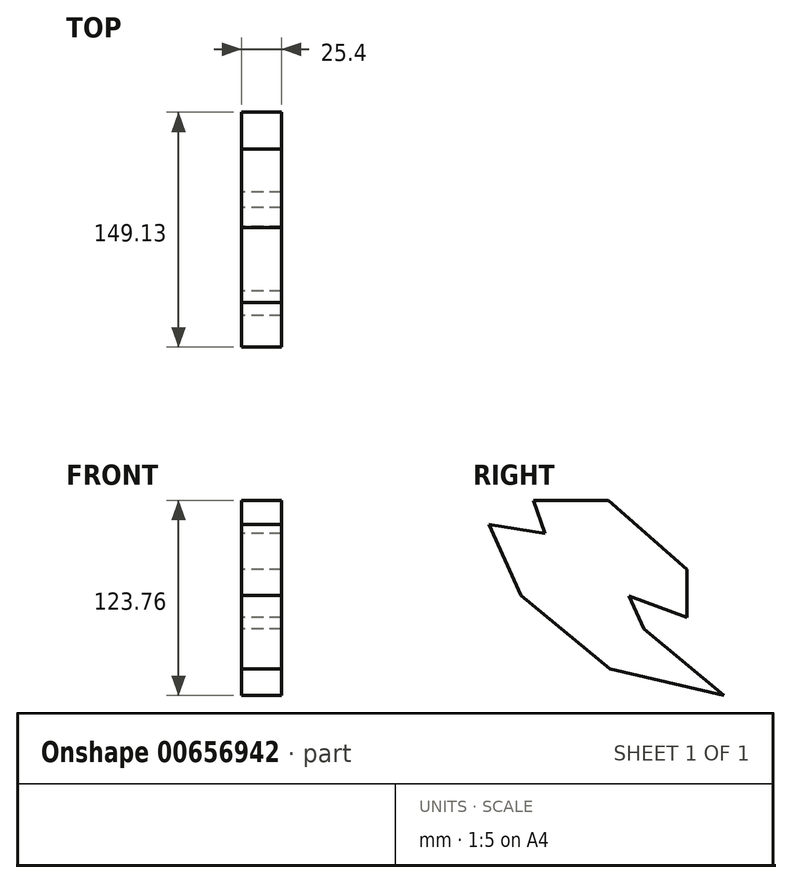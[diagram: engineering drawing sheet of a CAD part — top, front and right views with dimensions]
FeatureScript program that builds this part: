
annotation { "Feature Type Name" : "Feature", "Feature Type Description" : "" }
export const myFeature = defineFeature(function(context is Context, id is Id, definition is map)
    precondition{}
    {
        {
            var Q0;
            Q0=qCreatedBy(makeId("Right.planeOp"),FACE);
            var sketch = newSketch(context, id + "F0", { "sketchPlane" : qUnion([Q0])});
            skLineSegment(sketch, "E0", {"start": v(-23.38, 27.05) * mm, "end": v(24.18, 27.05) * mm});
            skLineSegment(sketch, "E1", {"start": v(24.18, 27.05) * mm, "end": v(74.16, -16.6) * mm});
            skLineSegment(sketch, "E2", {"start": v(74.16, -16.6) * mm, "end": v(74.16, -47.35) * mm});
            skLineSegment(sketch, "E3", {"start": v(74.16, -47.35) * mm, "end": v(37.08, -33.43) * mm});
            skLineSegment(sketch, "E4", {"start": v(37.08, -33.43) * mm, "end": v(46.75, -54.56) * mm});
            skLineSegment(sketch, "E5", {"start": v(46.75, -54.56) * mm, "end": v(97.54, -96.7) * mm});
            skLineSegment(sketch, "E6", {"start": v(97.54, -96.7) * mm, "end": v(24.99, -79.98) * mm});
            skLineSegment(sketch, "E7", {"start": v(24.99, -79.98) * mm, "end": v(-31.44, -33.15) * mm});
            skLineSegment(sketch, "E8", {"start": v(-31.44, -33.15) * mm, "end": v(-51.6, 11.83) * mm});
            skLineSegment(sketch, "E9", {"start": v(-51.6, 11.83) * mm, "end": v(-16.12, 6.2) * mm});
            skLineSegment(sketch, "E10", {"start": v(-16.12, 6.2) * mm, "end": v(-23.38, 27.05) * mm});
            skSolve(sketch);
        }
        {
            var Q0;
            Q0 = qSketchRegion(id + "F0", true);
            extrude(context, id + "F1", {"entities" : qUnion([Q0]), "depth" : 25.4 * mm, "offsetDistance" : 25.4 * mm});
        }
    });
